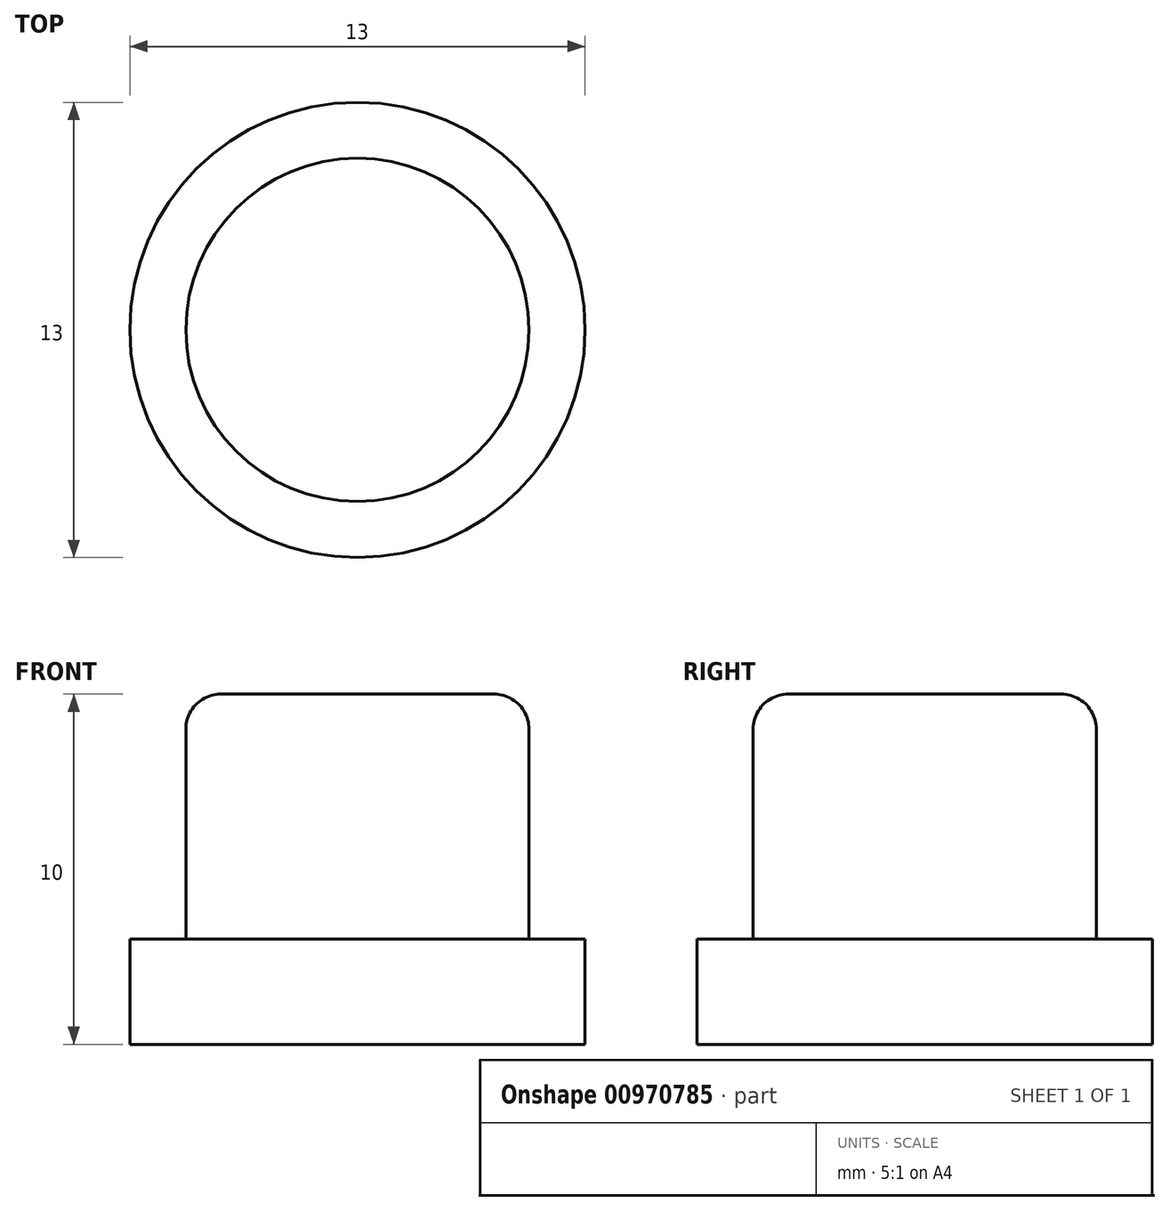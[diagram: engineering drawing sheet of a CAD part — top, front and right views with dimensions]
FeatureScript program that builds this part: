
annotation { "Feature Type Name" : "Feature", "Feature Type Description" : "" }
export const myFeature = defineFeature(function(context is Context, id is Id, definition is map)
    precondition{}
    {
        {
            var Q0;
            Q0=qCreatedBy(makeId("Top.planeOp"),FACE);
            var sketch = newSketch(context, id + "F0", { "sketchPlane" : qUnion([Q0])});
            skCircle(sketch, "E0", {"center": v(0, 0) * mm, "radius": 6.5 * mm});
            skSolve(sketch);
        }
        {
            var Q0;
            Q0 = qSketchRegion(id + "F0", true);
            extrude(context, id + "F1", {"entities" : qUnion([Q0]), "depth" : 3 * mm, "offsetDistance" : 25 * mm});
        }
        {
            var Q0;
            Q0=qCreatedBy(makeId("Top.planeOp"),FACE);
            var sketch = newSketch(context, id + "F2", { "sketchPlane" : qUnion([Q0])});
            skCircle(sketch, "E1", {"center": v(0, 0) * mm, "radius": 4.9 * mm});
            skSolve(sketch);
        }
        {
            var Q0;
            Q0 = qSketchRegion(id + "F2", true);
            extrude(context, id + "F3", {"entities" : qUnion([Q0]), "operationType" : NewBodyOperationType.ADD, "depth" : 10 * mm, "offsetDistance" : 25 * mm});
        }
        {
            var Q0;
            Q0=makeQuery(id+"F3.opExtrude","CAP_EDGE",EDGE,{"disambiguationData":[OSD([sQuery(id+"F2.wireOp",EDGE,"E1")])],"isStart":false});
            fillet(context, id + "F4", {"entities" : qUnion([Q0]), "radius" : 1 * mm, "tangentPropagation" : true, "allowEdgeOverflow" : false});
        }
    });
